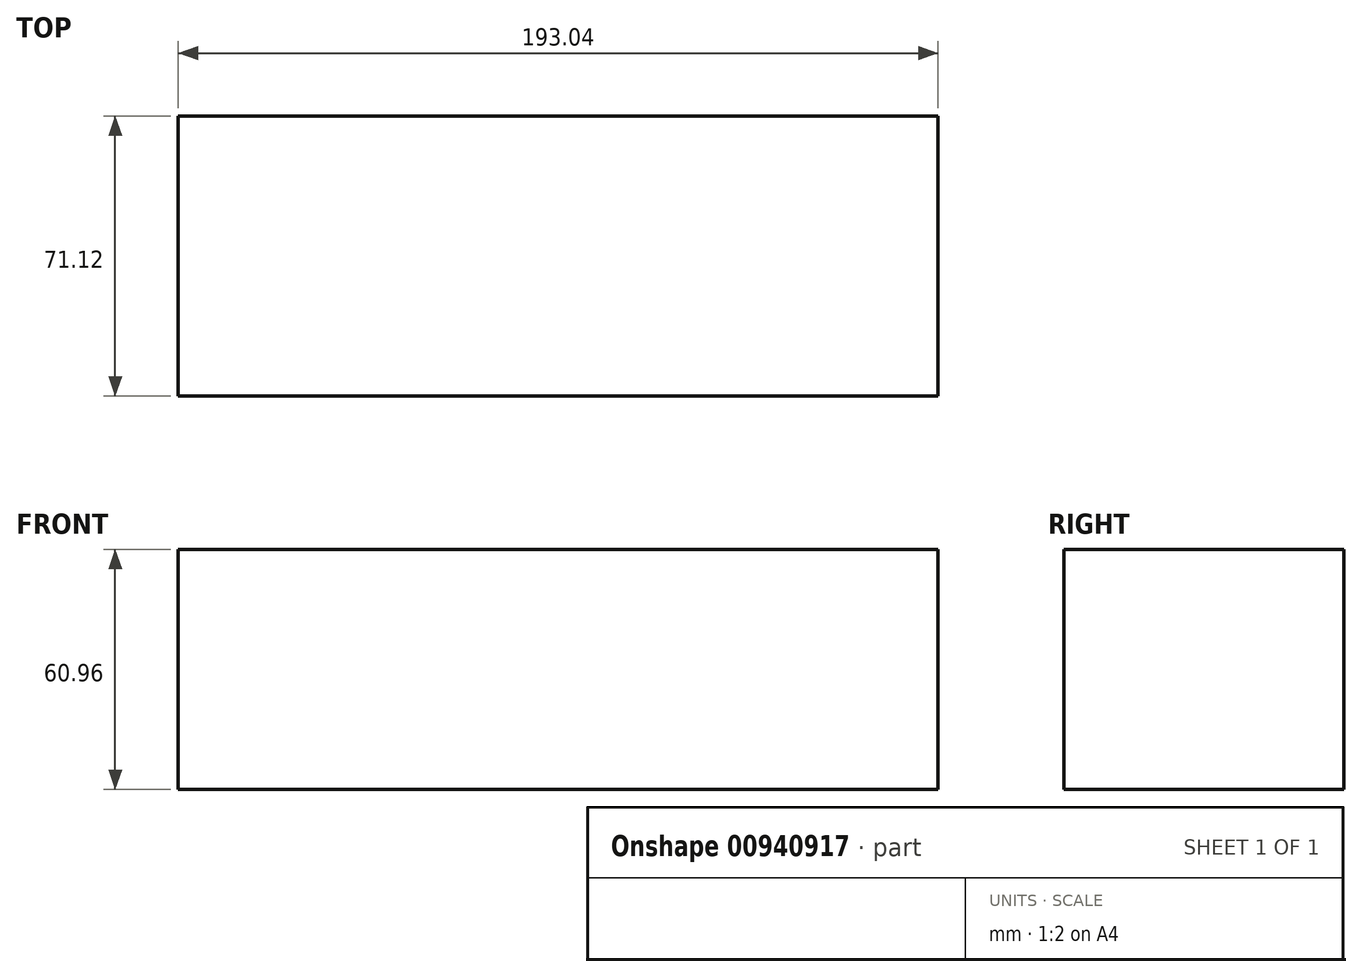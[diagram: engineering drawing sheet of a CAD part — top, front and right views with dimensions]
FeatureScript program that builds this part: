
annotation { "Feature Type Name" : "Feature", "Feature Type Description" : "" }
export const myFeature = defineFeature(function(context is Context, id is Id, definition is map)
    precondition{}
    {
        {
            var Q0;
            Q0=qCreatedBy(makeId("Top.planeOp"),FACE);
            var sketch = newSketch(context, id + "F0", { "sketchPlane" : qUnion([Q0])});
            skLineSegment(sketch, "E0.bottom", {"start": v(-96.52, 35.56) * mm, "end": v(96.52, 35.56) * mm});
            skLineSegment(sketch, "E0.top", {"start": v(-96.52, -35.56) * mm, "end": v(96.52, -35.56) * mm});
            skLineSegment(sketch, "E0.left", {"start": v(-96.52, 35.56) * mm, "end": v(-96.52, -35.56) * mm});
            skLineSegment(sketch, "E0.right", {"start": v(96.52, 35.56) * mm, "end": v(96.52, -35.56) * mm});
            skPoint(sketch, "E0.middle", {"position": v(0, 0) * mm});
            skSolve(sketch);
        }
        {
            var Q0;
            Q0=makeQuery(id+"F0.imprint","IMPRINT",FACE,{"disambiguationData":[TD([[makeQuery(id+"F0.imprint","IMPRINT",EDGE,{"derivedFrom":sQuery(id+"F0.wireOp",EDGE,"E0.bottom")}),-1.0]])]});
            extrude(context, id + "F1", {"entities" : qUnion([Q0]), "oppositeDirection" : true, "depth" : 60.96 * mm, "offsetDistance" : 25 * mm});
        }
    });
